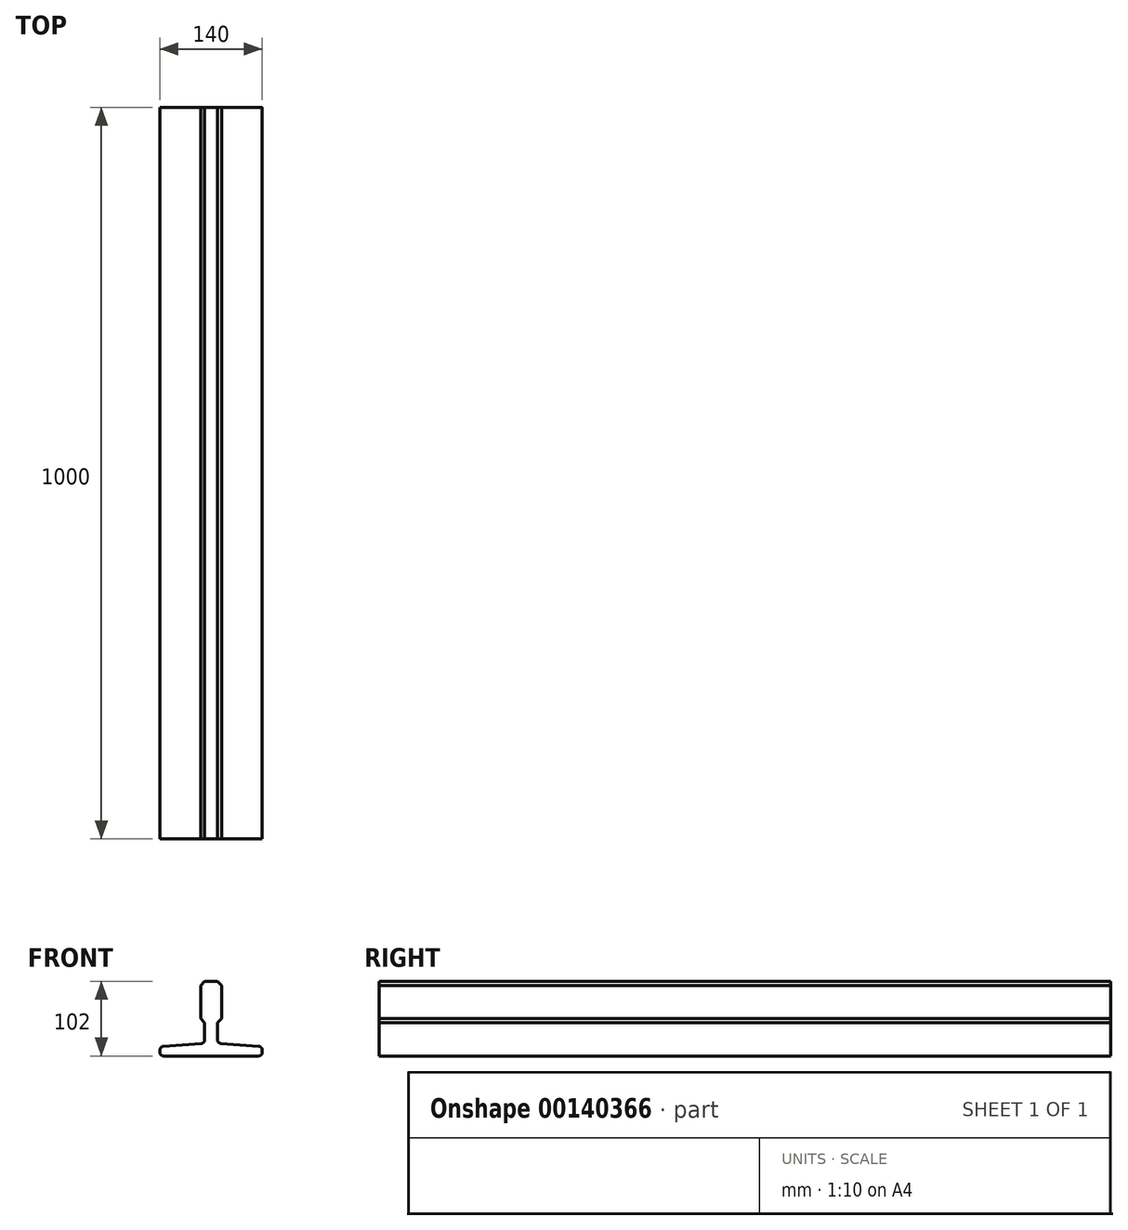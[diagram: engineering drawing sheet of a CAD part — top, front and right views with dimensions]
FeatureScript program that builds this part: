
annotation { "Feature Type Name" : "Feature", "Feature Type Description" : "" }
export const myFeature = defineFeature(function(context is Context, id is Id, definition is map)
    precondition{}
    {
        {
            var Q0;
            Q0=qCreatedBy(makeId("Front.planeOp"),FACE);
            var sketch = newSketch(context, id + "F0", { "sketchPlane" : qUnion([Q0])});
            skLineSegment(sketch, "E0", {"start": v(5, 0) * mm, "end": v(135, 0) * mm});
            skLineSegment(sketch, "E1", {"start": v(140, 5) * mm, "end": v(140, 8.08) * mm});
            skLineSegment(sketch, "E2", {"start": v(135.4, 13.06) * mm, "end": v(83.36, 17.14) * mm});
            skLineSegment(sketch, "E3", {"start": v(84.3, 51) * mm, "end": v(84.3, 96.45) * mm});
            skLineSegment(sketch, "E4", {"start": v(78.75, 102) * mm, "end": v(61.25, 102) * mm});
            skLineSegment(sketch, "E5", {"start": v(55.7, 96.45) * mm, "end": v(55.7, 51) * mm});
            skLineSegment(sketch, "E6", {"start": v(56.64, 17.14) * mm, "end": v(4.6, 13.06) * mm});
            skLineSegment(sketch, "E7", {"start": v(0, 8.08) * mm, "end": v(0, 5) * mm});
            skPoint(sketch, "E8.visualSharp", {"position": v(140, 12.7) * mm});
            skArc(sketch, "E8.filletArc", {"start": v(140, 8.08) * mm, "mid": v(138.67, 11.47) * mm, "end": v(135.4, 13.06) * mm});
            skPoint(sketch, "E9.visualSharp", {"position": v(140, 0) * mm});
            skArc(sketch, "E9.filletArc", {"start": v(135, 0) * mm, "mid": v(138.54, 1.46) * mm, "end": v(140, 5) * mm});
            skPoint(sketch, "E10.visualSharp", {"position": v(0, 12.7) * mm});
            skArc(sketch, "E10.filletArc", {"start": v(4.6, 13.06) * mm, "mid": v(1.33, 11.47) * mm, "end": v(0, 8.08) * mm});
            skPoint(sketch, "E11.visualSharp", {"position": v(0, 0) * mm});
            skArc(sketch, "E11.filletArc", {"start": v(0, 5) * mm, "mid": v(1.46, 1.46) * mm, "end": v(5, 0) * mm});
            skLineSegment(sketch, "E12", {"start": v(61.25, 22.12) * mm, "end": v(61.25, 45.45) * mm});
            skLineSegment(sketch, "E13", {"start": v(78.75, 22.12) * mm, "end": v(78.75, 45.45) * mm});
            skPoint(sketch, "E14.visualSharp", {"position": v(61.25, 17.5) * mm});
            skArc(sketch, "E14.filletArc", {"start": v(56.64, 17.14) * mm, "mid": v(59.92, 18.73) * mm, "end": v(61.25, 22.12) * mm});
            skPoint(sketch, "E15.visualSharp", {"position": v(78.75, 17.5) * mm});
            skArc(sketch, "E15.filletArc", {"start": v(78.75, 22.12) * mm, "mid": v(80.08, 18.73) * mm, "end": v(83.36, 17.14) * mm});
            skLineSegment(sketch, "E16", {"start": v(84.3, 51) * mm, "end": v(78.75, 45.45) * mm});
            skLineSegment(sketch, "E17", {"start": v(55.7, 51) * mm, "end": v(61.25, 45.45) * mm});
            skLineSegment(sketch, "E18", {"start": v(61.25, 102) * mm, "end": v(55.7, 96.45) * mm});
            skLineSegment(sketch, "E19", {"start": v(84.3, 96.45) * mm, "end": v(78.75, 102) * mm});
            skSolve(sketch);
        }
        {
            var Q0;
            Q0 = qSketchRegion(id + "F0", true);
            extrude(context, id + "F1", {"entities" : qUnion([Q0]), "oppositeDirection" : true, "depth" : 1000 * mm});
        }
    });
